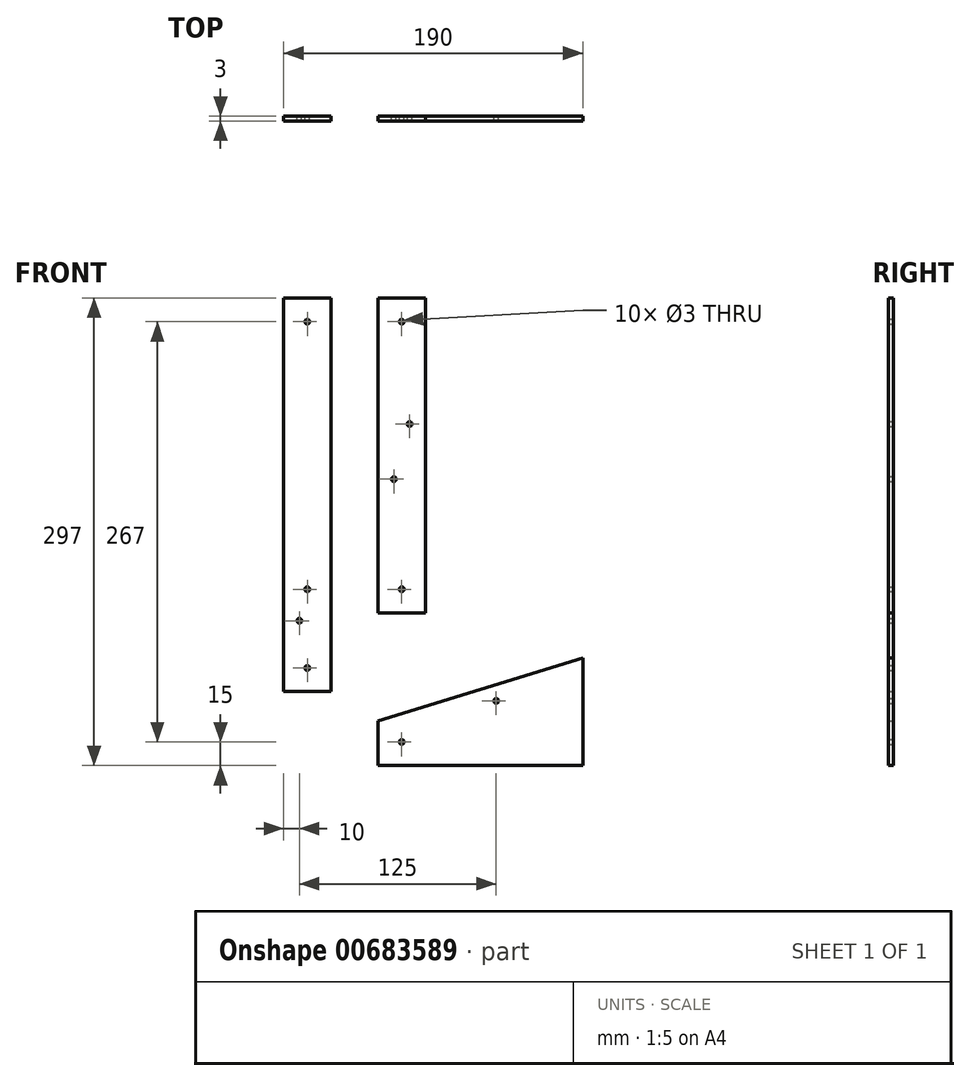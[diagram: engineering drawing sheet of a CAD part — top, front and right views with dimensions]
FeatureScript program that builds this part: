
annotation { "Feature Type Name" : "Feature", "Feature Type Description" : "" }
export const myFeature = defineFeature(function(context is Context, id is Id, definition is map)
    precondition{}
    {
        {
            var Q0;
            Q0=qCreatedBy(makeId("Front.planeOp"),FACE);
            var sketch = newSketch(context, id + "F0", { "sketchPlane" : qUnion([Q0])});
            skLineSegment(sketch, "E0.left", {"start": v(105, -148.5) * mm, "end": v(105, 148.5) * mm});
            skPoint(sketch, "E0.middle", {"position": v(0, 0) * mm});
            skLineSegment(sketch, "E1.bottom", {"start": v(-105, 148.5) * mm, "end": v(-75, 148.5) * mm});
            skLineSegment(sketch, "E1.top", {"start": v(-105, -101.5) * mm, "end": v(-75, -101.5) * mm});
            skLineSegment(sketch, "E1.left", {"start": v(-105, 148.5) * mm, "end": v(-105, -101.5) * mm});
            skLineSegment(sketch, "E1.right", {"start": v(-75, 148.5) * mm, "end": v(-75, -101.5) * mm});
            skLineSegment(sketch, "E2.bottom", {"start": v(-75, 148.5) * mm, "end": v(-45, 148.5) * mm});
            skLineSegment(sketch, "E2.top", {"start": v(-75, -101.5) * mm, "end": v(-45, -101.5) * mm});
            skLineSegment(sketch, "E2.right", {"start": v(-45, 148.5) * mm, "end": v(-45, -101.5) * mm});
            skLineSegment(sketch, "E3.bottom", {"start": v(-45, 148.5) * mm, "end": v(-15, 148.5) * mm});
            skLineSegment(sketch, "E3.top", {"start": v(-45, -51.5) * mm, "end": v(-15, -51.5) * mm});
            skLineSegment(sketch, "E3.left", {"start": v(-45, 148.5) * mm, "end": v(-45, -51.5) * mm});
            skLineSegment(sketch, "E3.right", {"start": v(-15, 148.5) * mm, "end": v(-15, -51.5) * mm});
            skLineSegment(sketch, "E4.bottom", {"start": v(-15, 148.5) * mm, "end": v(15, 148.5) * mm});
            skLineSegment(sketch, "E4.top", {"start": v(-15, -51.5) * mm, "end": v(15, -51.5) * mm});
            skLineSegment(sketch, "E4.right", {"start": v(15, 148.5) * mm, "end": v(15, -51.5) * mm});
            skCircle(sketch, "E5", {"center": v(-90, 133.5) * mm, "radius": 1.5 * mm});
            skPoint(sketch, "E5.centerSnap0", {"position": v(-90, 148.5) * mm});
            skLineSegment(sketch, "E6.bottom", {"start": v(-45, -51.5) * mm, "end": v(85, -51.5) * mm});
            skLineSegment(sketch, "E6.top", {"start": v(-45, -148.5) * mm, "end": v(85, -148.5) * mm});
            skLineSegment(sketch, "E6.left", {"start": v(-45, -51.5) * mm, "end": v(-45, -148.5) * mm});
            skLineSegment(sketch, "E6.right", {"start": v(85, -51.5) * mm, "end": v(85, -148.5) * mm});
            skLineSegment(sketch, "E7", {"start": v(-45, -120) * mm, "end": v(85, -80) * mm});
            skLineSegment(sketch, "E8.bottom", {"start": v(15, 148.5) * mm, "end": v(85, 148.5) * mm});
            skLineSegment(sketch, "E8.top", {"start": v(15, 78.5) * mm, "end": v(85, 78.5) * mm});
            skLineSegment(sketch, "E8.left", {"start": v(15, 148.5) * mm, "end": v(15, 78.5) * mm});
            skLineSegment(sketch, "E8.right", {"start": v(85, 148.5) * mm, "end": v(85, 78.5) * mm});
            skLineSegment(sketch, "E9.bottom", {"start": v(85, 78.5) * mm, "end": v(15, 78.5) * mm});
            skLineSegment(sketch, "E9.right", {"start": v(15, 78.5) * mm, "end": v(15, 8.5) * mm});
            skCircle(sketch, "E10", {"center": v(-30, 133.5) * mm, "radius": 1.5 * mm});
            skPoint(sketch, "E10.centerSnap0", {"position": v(-30, 148.5) * mm});
            skCircle(sketch, "E11", {"center": v(-30, -36.5) * mm, "radius": 1.5 * mm});
            skPoint(sketch, "E11.centerSnap0", {"position": v(-30, -51.5) * mm});
            skCircle(sketch, "E12", {"center": v(-90, -86.5) * mm, "radius": 1.5 * mm});
            skPoint(sketch, "E12.centerSnap0", {"position": v(-90, -101.5) * mm});
            skCircle(sketch, "E13", {"center": v(-90, -36.5) * mm, "radius": 1.5 * mm});
            skCircle(sketch, "E14", {"center": v(-95, -56.5) * mm, "radius": 1.5 * mm});
            skCircle(sketch, "E15", {"center": v(-35, 33.5) * mm, "radius": 1.5 * mm});
            skCircle(sketch, "E16", {"center": v(-25, 68.5) * mm, "radius": 1.5 * mm});
            skCircle(sketch, "E17", {"center": v(70, -66.5) * mm, "radius": 1.5 * mm});
            skCircle(sketch, "E18", {"center": v(10, -92.61) * mm, "radius": 1.5 * mm});
            skCircle(sketch, "E19", {"center": v(30, -107.39) * mm, "radius": 1.5 * mm});
            skCircle(sketch, "E20", {"center": v(-30, -133.5) * mm, "radius": 1.5 * mm});
            skCircle(sketch, "E21.MirrorC", {"center": v(-60, 133.5) * mm, "radius": 1.5 * mm});
            skCircle(sketch, "E22.MirrorC", {"center": v(-60, -36.5) * mm, "radius": 1.5 * mm});
            skCircle(sketch, "E23.MirrorC", {"center": v(-60, -86.5) * mm, "radius": 1.5 * mm});
            skCircle(sketch, "E24.MirrorC", {"center": v(0, -36.5) * mm, "radius": 1.5 * mm});
            skCircle(sketch, "E25.MirrorC", {"center": v(5, 33.5) * mm, "radius": 1.5 * mm});
            skCircle(sketch, "E26.MirrorC", {"center": v(-5, 68.5) * mm, "radius": 1.5 * mm});
            skCircle(sketch, "E27.MirrorC", {"center": v(0, 133.5) * mm, "radius": 1.5 * mm});
            skLineSegment(sketch, "E28.bottom", {"start": v(-105, -101.5) * mm, "end": v(-90, -101.5) * mm});
            skLineSegment(sketch, "E29.top", {"start": v(-90, -101.5) * mm, "end": v(-75, -101.5) * mm});
            skCircle(sketch, "E30.MirrorC", {"center": v(-55, -56.5) * mm, "radius": 1.5 * mm});
            skLineSegment(sketch, "E31", {"start": v(-105, -148.5) * mm, "end": v(-105, -101.5) * mm});
            skLineSegment(sketch, "E32", {"start": v(-45, -148.5) * mm, "end": v(-105, -148.5) * mm});
            skLineSegment(sketch, "E33", {"start": v(85, -148.5) * mm, "end": v(105, -148.5) * mm});
            skLineSegment(sketch, "E34", {"start": v(105, -148.5) * mm, "end": v(105, -128.5) * mm});
            skLineSegment(sketch, "E35", {"start": v(105, -128.5) * mm, "end": v(85, -128.5) * mm});
            skCircle(sketch, "E36", {"center": v(95, -138.5) * mm, "radius": 1.5 * mm});
            skPoint(sketch, "E36.centerSnap0", {"position": v(105, -138.5) * mm});
            skPoint(sketch, "E36.centerSnap1", {"position": v(95, -128.5) * mm});
            skCircle(sketch, "E37.0.1.0", {"center": v(95, -118.5) * mm, "radius": 1.5 * mm});
            skLineSegment(sketch, "E37.0.1.1", {"start": v(105, -108.5) * mm, "end": v(85, -108.5) * mm});
            skCircle(sketch, "E37.0.2.0", {"center": v(95, -98.5) * mm, "radius": 1.5 * mm});
            skLineSegment(sketch, "E37.0.2.1", {"start": v(105, -88.5) * mm, "end": v(85, -88.5) * mm});
            skCircle(sketch, "E37.0.3.0", {"center": v(95, -78.5) * mm, "radius": 1.5 * mm});
            skLineSegment(sketch, "E37.0.3.1", {"start": v(105, -68.5) * mm, "end": v(85, -68.5) * mm});
            skLineSegment(sketch, "E37.direction1", {"start": v(95, -138.5) * mm, "end": v(120, -138.5) * mm, "construction": true});
            skLineSegment(sketch, "E37.direction2", {"start": v(95, -138.5) * mm, "end": v(95, -118.5) * mm, "construction": true});
            skLineSegment(sketch, "E38", {"start": v(105, -68.5) * mm, "end": v(105, -128.5) * mm});
            skLineSegment(sketch, "E39", {"start": v(-75, -101.5) * mm, "end": v(-75, -148.5) * mm});
            skLineSegment(sketch, "E40", {"start": v(-75, -125) * mm, "end": v(-45, -125) * mm});
            skLineSegment(sketch, "E41", {"start": v(-105, -135) * mm, "end": v(-75, -135) * mm});
            skLineSegment(sketch, "E42", {"start": v(38.5, 78.5) * mm, "end": v(38.5, -51.5) * mm});
            skLineSegment(sketch, "E43", {"start": v(38.5, -51.5) * mm, "end": v(15, -51.5) * mm});
            skLineSegment(sketch, "E44", {"start": v(105, 148.5) * mm, "end": v(85, 148.5) * mm});
            skSolve(sketch);
        }
        {
            var Q0;
            Q0=makeQuery(id+"F0.imprint","IMPRINT",FACE,{"disambiguationData":[TD([[makeQuery(id+"F0.imprint","IMPRINT",EDGE,{"derivedFrom":sQuery(id+"F0.wireOp",EDGE,"E1.bottom")}),-1.0]])]});
            var Q1;
            Q1=makeQuery(id+"F0.imprint","IMPRINT",FACE,{"disambiguationData":[TD([[makeQuery(id+"F0.imprint","IMPRINT",EDGE,{"derivedFrom":sQuery(id+"F0.wireOp",EDGE,"E3.bottom")}),-1.0]])]});
            var Q2;
            {var subQ2=sQuery(id+"F0.wireOp",EDGE,"E6.top");Q2=makeQuery(id+"F0.imprint","IMPRINT",FACE,{"disambiguationData":[TD([[makeQuery(id+"F0.imprint","IMPRINT",EDGE,{"derivedFrom":subQ2}),1.0]])]});}
            extrude(context, id + "F1", {"entities" : qUnion([Q0, Q1, Q2]), "depth" : 3 * mm, "offsetDistance" : 25 * mm});
        }
    });
